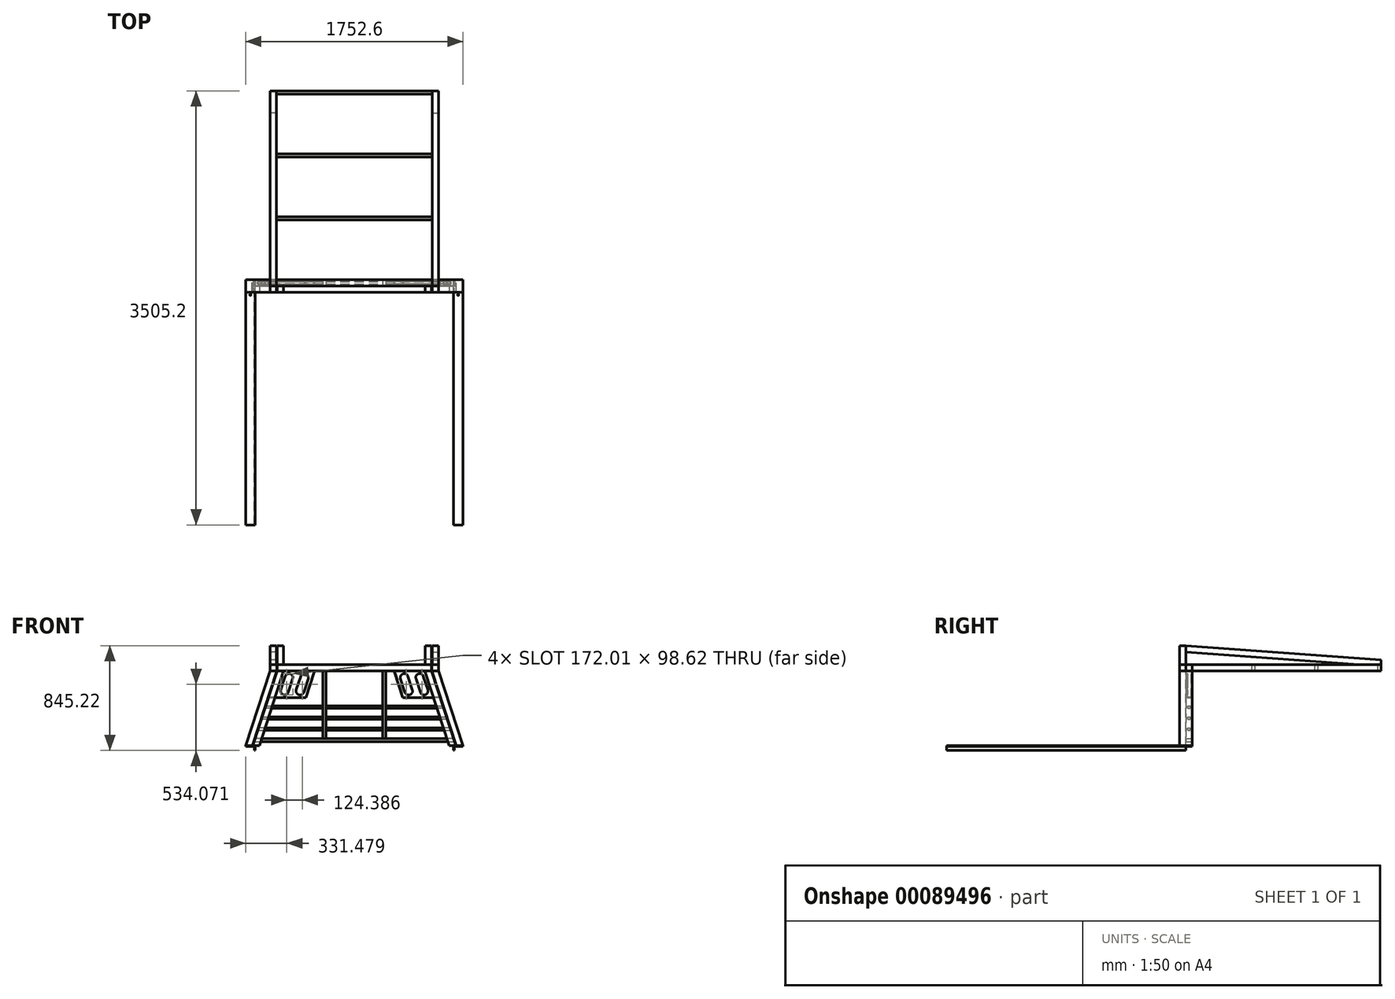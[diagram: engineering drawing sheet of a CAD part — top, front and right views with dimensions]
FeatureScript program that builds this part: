
annotation { "Feature Type Name" : "Feature", "Feature Type Description" : "" }
export const myFeature = defineFeature(function(context is Context, id is Id, definition is map)
    precondition{}
    {
        {
            var Q0;
            Q0=qCreatedBy(makeId("Front.planeOp"),FACE);
            var sketch = newSketch(context, id + "F0", { "sketchPlane" : qUnion([Q0])});
            skLineSegment(sketch, "E0", {"start": v(-876.3, 0) * mm, "end": v(-822.89, 0) * mm});
            skLineSegment(sketch, "E1", {"start": v(-822.89, 0) * mm, "end": v(-626.66, 603.92) * mm});
            skLineSegment(sketch, "E2", {"start": v(-626.66, 603.92) * mm, "end": v(-680.07, 603.92) * mm});
            skLineSegment(sketch, "E3", {"start": v(-680.07, 603.92) * mm, "end": v(-876.3, 0) * mm});
            skLineSegment(sketch, "E4", {"start": v(626.66, 603.92) * mm, "end": v(680.07, 603.92) * mm});
            skLineSegment(sketch, "E5", {"start": v(680.07, 603.92) * mm, "end": v(876.3, 0) * mm});
            skLineSegment(sketch, "E6", {"start": v(876.3, 0) * mm, "end": v(822.89, 0) * mm});
            skLineSegment(sketch, "E7", {"start": v(822.89, 0) * mm, "end": v(626.66, 603.92) * mm});
            skLineSegment(sketch, "E8", {"start": v(-822.89, 0) * mm, "end": v(822.89, 0) * mm, "construction": true});
            skSolve(sketch);
        }
        {
            var Q0;
            Q0 = qSketchRegion(id + "F0", true);
            extrude(context, id + "F1", {"entities" : qUnion([Q0]), "depth" : 76.2 * mm, "hasSecondDirection" : true, "secondDirectionOppositeDirection" : true, "secondDirectionDepth" : 25.4 * mm});
        }
        {
            var Q0;
            Q0=qCreatedBy(makeId("Front.planeOp"),FACE);
            var sketch = newSketch(context, id + "F2", { "sketchPlane" : qUnion([Q0])});
            skLineSegment(sketch, "E9", {"start": v(-680.07, 654.72) * mm, "end": v(680.07, 654.72) * mm});
            skLineSegment(sketch, "E10", {"start": v(680.07, 654.72) * mm, "end": v(680.07, 603.92) * mm});
            skLineSegment(sketch, "E11", {"start": v(680.07, 603.92) * mm, "end": v(-680.07, 603.92) * mm});
            skLineSegment(sketch, "E12", {"start": v(-680.07, 603.92) * mm, "end": v(-680.07, 654.72) * mm});
            skLineSegment(sketch, "E13", {"start": v(-812.57, 31.75) * mm, "end": v(812.57, 31.75) * mm});
            skLineSegment(sketch, "E14", {"start": v(812.57, 31.75) * mm, "end": v(804.32, 57.15) * mm});
            skLineSegment(sketch, "E15", {"start": v(804.32, 57.15) * mm, "end": v(-804.32, 57.15) * mm});
            skLineSegment(sketch, "E16", {"start": v(-804.32, 57.15) * mm, "end": v(-812.57, 31.75) * mm});
            skSolve(sketch);
        }
        {
            var Q0;
            Q0 = qSketchRegion(id + "F2", true);
            extrude(context, id + "F3", {"entities" : qUnion([Q0]), "depth" : 25.4 * mm, "hasSecondDirection" : true, "secondDirectionOppositeDirection" : true, "secondDirectionDepth" : 25.4 * mm});
        }
        {
            var Q0;
            Q0=makeQuery(id+"F1.opExtrude","CAP_FACE",FACE,{"disambiguationData":[OSD([sQuery(id+"F0.wireOp",EDGE,"E4"),sQuery(id+"F0.wireOp",EDGE,"E5"),sQuery(id+"F0.wireOp",EDGE,"E6"),sQuery(id+"F0.wireOp",EDGE,"E7")])],"isStart":true});
            var sketch = newSketch(context, id + "F4", { "sketchPlane" : qUnion([Q0])});
            skLineSegment(sketch, "E17", {"start": v(-626.66, 603.92) * mm, "end": v(-696.81, 388.02) * mm});
            skLineSegment(sketch, "E18", {"start": v(-696.81, 388.02) * mm, "end": v(-392.01, 388.02) * mm});
            skLineSegment(sketch, "E19", {"start": v(-392.01, 388.02) * mm, "end": v(-321.86, 603.92) * mm});
            skLineSegment(sketch, "E20", {"start": v(-321.86, 603.92) * mm, "end": v(-626.66, 603.92) * mm});
            skLineSegment(sketch, "E21", {"start": v(321.86, 603.92) * mm, "end": v(626.66, 603.92) * mm});
            skLineSegment(sketch, "E22", {"start": v(626.66, 603.92) * mm, "end": v(696.81, 388.02) * mm});
            skLineSegment(sketch, "E23", {"start": v(696.81, 388.02) * mm, "end": v(392.01, 388.02) * mm});
            skLineSegment(sketch, "E24", {"start": v(392.01, 388.02) * mm, "end": v(321.86, 603.92) * mm});
            skSolve(sketch);
        }
        {
            var Q0;
            Q0 = qSketchRegion(id + "F4", true);
            extrude(context, id + "F5", {"entities" : qUnion([Q0]), "oppositeDirection" : true, "depth" : 6.35 * mm});
        }
        {
            var Q0;
            Q0=makeQuery(id+"F5.opExtrude","CAP_FACE",FACE,{"disambiguationData":[OSD([sQuery(id+"F4.wireOp",EDGE,"E21"),sQuery(id+"F4.wireOp",EDGE,"E22"),sQuery(id+"F4.wireOp",EDGE,"E23"),sQuery(id+"F4.wireOp",EDGE,"E24")])],"isStart":false});
            var Q1;
            Q1=makeQuery(id+"F5.opExtrude","CAP_FACE",FACE,{"disambiguationData":[OSD([sQuery(id+"F4.wireOp",EDGE,"E17"),sQuery(id+"F4.wireOp",EDGE,"E18"),sQuery(id+"F4.wireOp",EDGE,"E19"),sQuery(id+"F4.wireOp",EDGE,"E20")])],"isStart":false});
            extrude(context, id + "F6", {"entities" : qUnion([Q0, Q1]), "depth" : 38.1 * mm, "hasSecondDirection" : true, "secondDirectionOppositeDirection" : false, "secondDirectionDepth" : 31.75 * mm});
        }
        {
            var Q0;
            Q0=makeQuery(id+"F5.opExtrude","CAP_FACE",FACE,{"disambiguationData":[OSD([sQuery(id+"F4.wireOp",EDGE,"E21"),sQuery(id+"F4.wireOp",EDGE,"E22"),sQuery(id+"F4.wireOp",EDGE,"E23"),sQuery(id+"F4.wireOp",EDGE,"E24")])],"isStart":false});
            var sketch = newSketch(context, id + "F7", { "sketchPlane" : qUnion([Q0])});
            skLineSegment(sketch, "E25", {"start": v(-321.86, 603.92) * mm, "end": v(-392.01, 388.02) * mm});
            skLineSegment(sketch, "E26", {"start": v(-392.01, 388.02) * mm, "end": v(-398.69, 388.02) * mm});
            skLineSegment(sketch, "E27", {"start": v(-398.69, 388.02) * mm, "end": v(-328.54, 603.92) * mm});
            skLineSegment(sketch, "E28", {"start": v(-328.54, 603.92) * mm, "end": v(-321.86, 603.92) * mm});
            skLineSegment(sketch, "E29", {"start": v(321.86, 603.92) * mm, "end": v(392.01, 388.02) * mm});
            skLineSegment(sketch, "E30", {"start": v(392.01, 388.02) * mm, "end": v(398.69, 388.02) * mm});
            skLineSegment(sketch, "E31", {"start": v(398.69, 388.02) * mm, "end": v(328.54, 603.92) * mm});
            skLineSegment(sketch, "E32", {"start": v(328.54, 603.92) * mm, "end": v(321.86, 603.92) * mm});
            skSolve(sketch);
        }
        {
            var Q0;
            Q0 = qSketchRegion(id + "F7", true);
            var Q1;
            Q1=makeQuery(id+"F6.opExtrude","CAP_FACE",FACE,{"disambiguationData":[OSD([sQuery(id+"F4.wireOp",EDGE,"E21"),sQuery(id+"F4.wireOp",EDGE,"E22"),sQuery(id+"F4.wireOp",EDGE,"E23"),sQuery(id+"F4.wireOp",EDGE,"E24")])],"isStart":true});
            extrude(context, id + "F8", {"entities" : qUnion([Q0]), "endBound" : BoundingType.UP_TO_SURFACE, "endBoundEntityFace" : qUnion([Q1]), "depth" : 25.4 * mm});
        }
        {
            var Q0;
            Q0=makeQuery(id+"F5.opExtrude","CAP_FACE",FACE,{"disambiguationData":[OSD([sQuery(id+"F4.wireOp",EDGE,"E21"),sQuery(id+"F4.wireOp",EDGE,"E22"),sQuery(id+"F4.wireOp",EDGE,"E23"),sQuery(id+"F4.wireOp",EDGE,"E24")])],"isStart":false});
            var sketch = newSketch(context, id + "F9", { "sketchPlane" : qUnion([Q0])});
            skLineSegment(sketch, "E33", {"start": v(-696.81, 388.02) * mm, "end": v(-398.69, 388.02) * mm});
            skLineSegment(sketch, "E34", {"start": v(-398.69, 388.02) * mm, "end": v(-396.62, 394.37) * mm});
            skLineSegment(sketch, "E35", {"start": v(-396.62, 394.37) * mm, "end": v(-694.75, 394.37) * mm});
            skLineSegment(sketch, "E36", {"start": v(-694.75, 394.37) * mm, "end": v(-696.81, 388.02) * mm});
            skLineSegment(sketch, "E37", {"start": v(398.69, 388.02) * mm, "end": v(696.81, 388.02) * mm});
            skLineSegment(sketch, "E38", {"start": v(696.81, 388.02) * mm, "end": v(694.75, 394.37) * mm});
            skLineSegment(sketch, "E39", {"start": v(694.75, 394.37) * mm, "end": v(396.62, 394.37) * mm});
            skLineSegment(sketch, "E40", {"start": v(396.62, 394.37) * mm, "end": v(398.69, 388.02) * mm});
            skSolve(sketch);
        }
        {
            var Q0;
            Q0 = qSketchRegion(id + "F9", true);
            extrude(context, id + "F10", {"entities" : qUnion([Q0]), "endBound" : BoundingType.UP_TO_NEXT, "depth" : 25.4 * mm});
        }
        {
            var Q0;
            Q0=makeQuery(id+"F6.opExtrude","CAP_FACE",FACE,{"disambiguationData":[OSD([sQuery(id+"F4.wireOp",EDGE,"E21"),sQuery(id+"F4.wireOp",EDGE,"E22"),sQuery(id+"F4.wireOp",EDGE,"E23"),sQuery(id+"F4.wireOp",EDGE,"E24")])],"isStart":false});
            var sketch = newSketch(context, id + "F11", { "sketchPlane" : qUnion([Q0])});
            skLineSegment(sketch, "E41", {"start": v(-438.1, 441.62) * mm, "end": v(-402.77, 550.32) * mm, "construction": true});
            skLineSegment(sketch, "E42", {"start": v(-562.48, 441.62) * mm, "end": v(-527.16, 550.32) * mm, "construction": true});
            skLineSegment(sketch, "E43", {"start": v(402.77, 550.32) * mm, "end": v(438.1, 441.62) * mm, "construction": true});
            skLineSegment(sketch, "E44", {"start": v(527.16, 550.32) * mm, "end": v(562.48, 441.62) * mm, "construction": true});
            skArc(sketch, "E45", {"start": v(-468.3, 451.43) * mm, "mid": v(-447.9, 411.42) * mm, "end": v(-407.9, 431.8) * mm});
            skArc(sketch, "E46", {"start": v(-372.58, 540.51) * mm, "mid": v(-392.96, 580.52) * mm, "end": v(-432.97, 560.14) * mm});
            skArc(sketch, "E47", {"start": v(-592.68, 451.43) * mm, "mid": v(-572.3, 411.42) * mm, "end": v(-532.29, 431.8) * mm});
            skArc(sketch, "E48", {"start": v(-496.96, 540.51) * mm, "mid": v(-517.35, 580.52) * mm, "end": v(-557.36, 560.14) * mm});
            skArc(sketch, "E49", {"start": v(432.97, 560.14) * mm, "mid": v(392.96, 580.52) * mm, "end": v(372.58, 540.51) * mm});
            skArc(sketch, "E50", {"start": v(407.9, 431.8) * mm, "mid": v(447.9, 411.42) * mm, "end": v(468.3, 451.43) * mm});
            skArc(sketch, "E51", {"start": v(557.36, 560.14) * mm, "mid": v(517.35, 580.52) * mm, "end": v(496.96, 540.51) * mm});
            skArc(sketch, "E52", {"start": v(532.29, 431.8) * mm, "mid": v(572.3, 411.42) * mm, "end": v(592.68, 451.43) * mm});
            skLineSegment(sketch, "E53", {"start": v(-468.3, 451.43) * mm, "end": v(-432.97, 560.14) * mm});
            skLineSegment(sketch, "E54", {"start": v(-372.58, 540.51) * mm, "end": v(-407.9, 431.8) * mm});
            skLineSegment(sketch, "E55", {"start": v(-532.29, 431.8) * mm, "end": v(-496.96, 540.51) * mm});
            skLineSegment(sketch, "E56", {"start": v(-592.68, 451.43) * mm, "end": v(-557.36, 560.14) * mm});
            skLineSegment(sketch, "E57", {"start": v(432.97, 560.14) * mm, "end": v(468.3, 451.43) * mm});
            skLineSegment(sketch, "E58", {"start": v(372.58, 540.51) * mm, "end": v(407.9, 431.8) * mm});
            skLineSegment(sketch, "E59", {"start": v(496.96, 540.51) * mm, "end": v(532.29, 431.8) * mm});
            skLineSegment(sketch, "E60", {"start": v(557.36, 560.14) * mm, "end": v(592.68, 451.43) * mm});
            skLineSegment(sketch, "E61", {"start": v(-608.32, 495.97) * mm, "end": v(-544.82, 495.97) * mm, "construction": true});
            skLineSegment(sketch, "E62", {"start": v(-544.82, 495.97) * mm, "end": v(-420.44, 495.97) * mm, "construction": true});
            skLineSegment(sketch, "E63", {"start": v(-420.44, 495.97) * mm, "end": v(-356.94, 495.97) * mm, "construction": true});
            skLineSegment(sketch, "E64", {"start": v(356.94, 495.97) * mm, "end": v(420.44, 495.97) * mm, "construction": true});
            skPoint(sketch, "E64.startSnap0", {"position": v(544.82, 495.97) * mm});
            skPoint(sketch, "E64.endSnap0", {"position": v(420.44, 495.97) * mm});
            skLineSegment(sketch, "E65", {"start": v(420.44, 495.97) * mm, "end": v(544.82, 495.97) * mm, "construction": true});
            skLineSegment(sketch, "E66", {"start": v(608.32, 495.97) * mm, "end": v(544.82, 495.97) * mm, "construction": true});
            skSolve(sketch);
        }
        {
            var Q0;
            Q0 = qSketchRegion(id + "F11", true);
            extrude(context, id + "F12", {"entities" : qUnion([Q0]), "operationType" : NewBodyOperationType.REMOVE, "endBound" : BoundingType.UP_TO_NEXT, "oppositeDirection" : true, "depth" : 25.4 * mm});
        }
        {
            var Q0;
            Q0=qCreatedBy(makeId("Front.planeOp"),FACE);
            var sketch = newSketch(context, id + "F13", { "sketchPlane" : qUnion([Q0])});
            skLineSegment(sketch, "E67", {"start": v(-782.08, 125.58) * mm, "end": v(782.08, 125.58) * mm});
            skLineSegment(sketch, "E68", {"start": v(782.08, 125.58) * mm, "end": v(775.9, 144.63) * mm});
            skLineSegment(sketch, "E69", {"start": v(775.9, 144.63) * mm, "end": v(-775.9, 144.63) * mm});
            skLineSegment(sketch, "E70", {"start": v(-775.9, 144.63) * mm, "end": v(-782.08, 125.58) * mm});
            skLineSegment(sketch, "E71", {"start": v(-753.66, 213.06) * mm, "end": v(-747.47, 232.11) * mm});
            skLineSegment(sketch, "E72", {"start": v(-747.47, 232.11) * mm, "end": v(747.47, 232.11) * mm});
            skLineSegment(sketch, "E73", {"start": v(747.47, 232.11) * mm, "end": v(753.66, 213.06) * mm});
            skLineSegment(sketch, "E74", {"start": v(753.66, 213.06) * mm, "end": v(-753.66, 213.06) * mm});
            skLineSegment(sketch, "E75", {"start": v(-725.23, 300.54) * mm, "end": v(-719.04, 319.6) * mm});
            skLineSegment(sketch, "E76", {"start": v(-719.04, 319.6) * mm, "end": v(719.04, 319.6) * mm});
            skLineSegment(sketch, "E77", {"start": v(719.04, 319.6) * mm, "end": v(725.23, 300.54) * mm});
            skLineSegment(sketch, "E78", {"start": v(725.23, 300.54) * mm, "end": v(-725.23, 300.54) * mm});
            skLineSegment(sketch, "E79", {"start": v(-392.01, 388.02) * mm, "end": v(392.01, 388.02) * mm, "construction": true});
            skLineSegment(sketch, "E80", {"start": v(0, 388.02) * mm, "end": v(0, 319.6) * mm, "construction": true});
            skLineSegment(sketch, "E81", {"start": v(0, 300.54) * mm, "end": v(0, 232.11) * mm, "construction": true});
            skLineSegment(sketch, "E82", {"start": v(0, 213.06) * mm, "end": v(0, 144.63) * mm, "construction": true});
            skLineSegment(sketch, "E83", {"start": v(0, 125.58) * mm, "end": v(0, 57.15) * mm, "construction": true});
            skSolve(sketch);
        }
        {
            var Q0;
            Q0 = qSketchRegion(id + "F13", true);
            extrude(context, id + "F14", {"entities" : qUnion([Q0]), "depth" : 9.52 * mm, "hasSecondDirection" : true, "secondDirectionOppositeDirection" : true, "secondDirectionDepth" : 9.52 * mm});
        }
        {
            var Q0;
            Q0=makeQuery(id+"F1.opExtrude","SWEPT_FACE",FACE,{"disambiguationData":[OSD([sQuery(id+"F0.wireOp",EDGE,"E0")])]});
            shell(context, id + "F15", {"entities" : qUnion([Q0]), "thickness" : 3.17 * mm});
        }
        {
            var Q0;
            Q0=makeQuery(id+"F1.opExtrude","CAP_FACE",FACE,{"disambiguationData":[OSD([sQuery(id+"F0.wireOp",EDGE,"E0"),sQuery(id+"F0.wireOp",EDGE,"E1"),sQuery(id+"F0.wireOp",EDGE,"E2"),sQuery(id+"F0.wireOp",EDGE,"E3")])],"isStart":true});
            var sketch = newSketch(context, id + "F16", { "sketchPlane" : qUnion([Q0])});
            skLineSegment(sketch, "E84", {"start": v(876.3, -6.35) * mm, "end": v(806.45, -6.35) * mm});
            skLineSegment(sketch, "E85", {"start": v(806.45, -6.35) * mm, "end": v(806.45, -38.1) * mm});
            skLineSegment(sketch, "E86", {"start": v(806.45, -38.1) * mm, "end": v(800.1, -38.1) * mm});
            skLineSegment(sketch, "E87", {"start": v(800.1, -38.1) * mm, "end": v(800.1, 0) * mm});
            skLineSegment(sketch, "E88", {"start": v(800.1, 0) * mm, "end": v(876.3, 0) * mm});
            skLineSegment(sketch, "E89", {"start": v(876.3, 0) * mm, "end": v(876.3, -6.35) * mm});
            skLineSegment(sketch, "E90", {"start": v(-876.3, 0) * mm, "end": v(-800.1, 0) * mm});
            skLineSegment(sketch, "E91", {"start": v(-800.1, 0) * mm, "end": v(-800.1, -38.1) * mm});
            skLineSegment(sketch, "E92", {"start": v(-800.1, -38.1) * mm, "end": v(-806.45, -38.1) * mm});
            skLineSegment(sketch, "E93", {"start": v(-806.45, -38.1) * mm, "end": v(-806.45, -6.35) * mm});
            skLineSegment(sketch, "E94", {"start": v(-806.45, -6.35) * mm, "end": v(-876.3, -6.35) * mm});
            skLineSegment(sketch, "E95", {"start": v(-876.3, -6.35) * mm, "end": v(-876.3, 0) * mm});
            skSolve(sketch);
        }
        {
            var Q0;
            Q0 = qSketchRegion(id + "F16", true);
            extrude(context, id + "F17", {"entities" : qUnion([Q0]), "oppositeDirection" : true, "depth" : 1828.8 * mm + 152.4 * mm});
        }
        {
            var Q0;
            Q0=makeQuery(id+"F17.opExtrude","SWEPT_FACE",FACE,{"disambiguationData":[OSD([sQuery(id+"F16.wireOp",EDGE,"E93")])]});
            var sketch = newSketch(context, id + "F18", { "sketchPlane" : qUnion([Q0])});
            skLineSegment(sketch, "E96.bottom", {"start": v(25.4, -38.1) * mm, "end": v(-25.4, -38.1) * mm});
            skLineSegment(sketch, "E96.top", {"start": v(25.4, -6.35) * mm, "end": v(-25.4, -6.35) * mm});
            skLineSegment(sketch, "E96.left", {"start": v(25.4, -38.1) * mm, "end": v(25.4, -6.35) * mm});
            skLineSegment(sketch, "E96.right", {"start": v(-25.4, -38.1) * mm, "end": v(-25.4, -6.35) * mm});
            skSolve(sketch);
        }
        {
            var Q0;
            Q0 = qSketchRegion(id + "F18", true);
            extrude(context, id + "F19", {"entities" : qUnion([Q0]), "operationType" : NewBodyOperationType.REMOVE, "endBound" : BoundingType.THROUGH_ALL, "oppositeDirection" : true, "depth" : 25.4 * mm});
        }
        {
            var Q0;
            Q0=makeQuery(id+"F17.opExtrude","SWEPT_FACE",FACE,{"disambiguationData":[OSD([sQuery(id+"F16.wireOp",EDGE,"E95")])]});
            var Q1;
            Q1=makeQuery(id+"F17.opExtrude","SWEPT_FACE",FACE,{"disambiguationData":[OSD([sQuery(id+"F16.wireOp",EDGE,"E91")])]});
            cPlane(context, id + "F20", {"entities" : qUnion([Q0, Q1]), "cplaneType" : CPlaneType.MID_PLANE, "offset" : 25.4 * mm, "width" : 152.4 * mm, "height" : 152.4 * mm});
        }
        {
            var Q0;
            Q0=makeQuery(id+"F17.opExtrude","SWEPT_FACE",FACE,{"disambiguationData":[OSD([sQuery(id+"F16.wireOp",EDGE,"E87")])]});
            var Q1;
            Q1=makeQuery(id+"F17.opExtrude","SWEPT_FACE",FACE,{"disambiguationData":[OSD([sQuery(id+"F16.wireOp",EDGE,"E89")])]});
            cPlane(context, id + "F21", {"entities" : qUnion([Q0, Q1]), "cplaneType" : CPlaneType.MID_PLANE, "offset" : 25.4 * mm, "width" : 152.4 * mm, "height" : 152.4 * mm});
        }
        {
            var Q0;
            Q0=makeQuery(id+"F19.boolean.opBoolean","MERGE",FACE,{"derivedFrom":[makeQuery(id+"F17.opExtrude","SWEPT_FACE",FACE,{"disambiguationData":[OSD([sQuery(id+"F16.wireOp",EDGE,"E94")])]}),makeQuery(id+"F19.opExtrude","SWEPT_FACE",FACE,{"disambiguationData":[OSD([sQuery(id+"F18.wireOp",EDGE,"E96.top")])]})]});
            var sketch = newSketch(context, id + "F22", { "sketchPlane" : qUnion([Q0])});
            skCircle(sketch, "E97", {"center": v(-838.2, 98.42) * mm, "radius": 5.04 * mm});
            skCircle(sketch, "E98", {"center": v(838.2, 98.43) * mm, "radius": 5.04 * mm});
            skLineSegment(sketch, "E99", {"start": v(-838.2, 98.42) * mm, "end": v(838.2, 98.43) * mm, "construction": true});
            skLineSegment(sketch, "E100", {"start": v(0, 98.43) * mm, "end": v(0, -25.4) * mm, "construction": true});
            skSolve(sketch);
        }
        {
            var Q0;
            Q0 = qSketchRegion(id + "F22", true);
            extrude(context, id + "F23", {"entities" : qUnion([Q0]), "operationType" : NewBodyOperationType.REMOVE, "endBound" : BoundingType.UP_TO_NEXT, "oppositeDirection" : true, "depth" : 25.4 * mm});
        }
        {
            var Q0;
            Q0=makeQuery(id+"F3.opExtrude","CAP_FACE",FACE,{"disambiguationData":[OSD([sQuery(id+"F2.wireOp",EDGE,"E9"),sQuery(id+"F2.wireOp",EDGE,"E10"),sQuery(id+"F2.wireOp",EDGE,"E11"),sQuery(id+"F2.wireOp",EDGE,"E12")])],"isStart":false});
            var sketch = newSketch(context, id + "F24", { "sketchPlane" : qUnion([Q0])});
            skLineSegment(sketch, "E101.bottom", {"start": v(-680.07, 654.72) * mm, "end": v(-626.66, 654.72) * mm});
            skLineSegment(sketch, "E101.top", {"start": v(-680.07, 603.92) * mm, "end": v(-626.66, 603.92) * mm});
            skLineSegment(sketch, "E101.left", {"start": v(-680.07, 654.72) * mm, "end": v(-680.07, 603.92) * mm});
            skLineSegment(sketch, "E101.right", {"start": v(-626.66, 654.72) * mm, "end": v(-626.66, 603.92) * mm});
            skLineSegment(sketch, "E102.bottom", {"start": v(680.07, 603.92) * mm, "end": v(626.66, 603.92) * mm});
            skLineSegment(sketch, "E102.top", {"start": v(680.07, 654.72) * mm, "end": v(626.66, 654.72) * mm});
            skLineSegment(sketch, "E102.left", {"start": v(680.07, 603.92) * mm, "end": v(680.07, 654.72) * mm});
            skLineSegment(sketch, "E102.right", {"start": v(626.66, 603.92) * mm, "end": v(626.66, 654.72) * mm});
            skSolve(sketch);
        }
        {
            var Q0;
            Q0 = qSketchRegion(id + "F24", true);
            extrude(context, id + "F25", {"entities" : qUnion([Q0]), "depth" : 50.8 * mm});
        }
        {
            var Q0;
            Q0=makeQuery(id+"F25.opExtrude","CAP_FACE",FACE,{"disambiguationData":[OSD([sQuery(id+"F24.wireOp",EDGE,"E101.bottom"),sQuery(id+"F24.wireOp",EDGE,"E101.top"),sQuery(id+"F24.wireOp",EDGE,"E101.left"),sQuery(id+"F24.wireOp",EDGE,"E101.right")])],"isStart":false});
            var sketch = newSketch(context, id + "F26", { "sketchPlane" : qUnion([Q0])});
            skLineSegment(sketch, "E103.bottom", {"start": v(-680.07, 654.72) * mm, "end": v(-629.27, 654.72) * mm});
            skLineSegment(sketch, "E103.top", {"start": v(-680.07, 807.12) * mm, "end": v(-629.27, 807.12) * mm});
            skLineSegment(sketch, "E103.left", {"start": v(-680.07, 654.72) * mm, "end": v(-680.07, 807.12) * mm});
            skLineSegment(sketch, "E103.right", {"start": v(-629.27, 654.72) * mm, "end": v(-629.27, 807.12) * mm});
            skLineSegment(sketch, "E104.bottom", {"start": v(680.07, 654.72) * mm, "end": v(629.27, 654.72) * mm});
            skLineSegment(sketch, "E104.top", {"start": v(680.07, 807.12) * mm, "end": v(629.27, 807.12) * mm});
            skLineSegment(sketch, "E104.left", {"start": v(680.07, 654.72) * mm, "end": v(680.07, 807.12) * mm});
            skLineSegment(sketch, "E104.right", {"start": v(629.27, 654.72) * mm, "end": v(629.27, 807.12) * mm});
            skSolve(sketch);
        }
        {
            var Q0;
            Q0 = qSketchRegion(id + "F26", true);
            extrude(context, id + "F27", {"entities" : qUnion([Q0]), "oppositeDirection" : true, "depth" : 50.8 * mm});
        }
        {
            var Q0;
            Q0=makeQuery(id+"F27.opExtrude","SWEPT_FACE",FACE,{"disambiguationData":[OSD([sQuery(id+"F26.wireOp",EDGE,"E104.left")])]});
            var sketch = newSketch(context, id + "F28", { "sketchPlane" : qUnion([Q0])});
            skLineSegment(sketch, "E105.bottom", {"start": v(25.4, 603.92) * mm, "end": v(1549.4, 603.92) * mm});
            skLineSegment(sketch, "E105.top", {"start": v(25.4, 654.72) * mm, "end": v(1549.4, 654.72) * mm});
            skLineSegment(sketch, "E105.left", {"start": v(25.4, 603.92) * mm, "end": v(25.4, 654.72) * mm});
            skLineSegment(sketch, "E105.right", {"start": v(1549.4, 603.92) * mm, "end": v(1549.4, 654.72) * mm});
            skSolve(sketch);
        }
        {
            var Q0;
            Q0 = qSketchRegion(id + "F28", true);
            extrude(context, id + "F29", {"entities" : qUnion([Q0]), "oppositeDirection" : true, "depth" : 50.8 * mm});
        }
        {
            var Q0;
            Q0=makeQuery(id+"F29.opExtrude","CAP_FACE",FACE,{"disambiguationData":[OSD([sQuery(id+"F28.wireOp",EDGE,"E105.bottom"),sQuery(id+"F28.wireOp",EDGE,"E105.top"),sQuery(id+"F28.wireOp",EDGE,"E105.left"),sQuery(id+"F28.wireOp",EDGE,"E105.right")])],"isStart":true});
            var sketch = newSketch(context, id + "F30", { "sketchPlane" : qUnion([Q0])});
            skLineSegment(sketch, "E106", {"start": v(1372.58, 654.72) * mm, "end": v(-25.4, 756.19) * mm});
            skLineSegment(sketch, "E107", {"start": v(-25.4, 756.19) * mm, "end": v(-25.4, 807.12) * mm});
            skLineSegment(sketch, "E108", {"start": v(-25.4, 807.12) * mm, "end": v(1549.4, 692.82) * mm});
            skLineSegment(sketch, "E109", {"start": v(1549.4, 692.82) * mm, "end": v(1549.4, 654.72) * mm});
            skLineSegment(sketch, "E110", {"start": v(1549.4, 654.72) * mm, "end": v(1372.58, 654.72) * mm});
            skSolve(sketch);
        }
        {
            var Q0;
            Q0 = qSketchRegion(id + "F30", true);
            extrude(context, id + "F31", {"entities" : qUnion([Q0]), "oppositeDirection" : true, "depth" : 50.8 * mm});
        }
        {
            var Q0;
            Q0=makeQuery(id+"F31.opExtrude","SWEPT_BODY",BODY,{"disambiguationData":[OSD([sQuery(id+"F30.wireOp",EDGE,"E106"),sQuery(id+"F30.wireOp",EDGE,"E107"),sQuery(id+"F30.wireOp",EDGE,"E108"),sQuery(id+"F30.wireOp",EDGE,"E109"),sQuery(id+"F30.wireOp",EDGE,"E110")])]});
            var Q1;
            Q1=makeQuery(id+"F29.opExtrude","SWEPT_BODY",BODY,{"disambiguationData":[OSD([sQuery(id+"F28.wireOp",EDGE,"E105.bottom"),sQuery(id+"F28.wireOp",EDGE,"E105.top"),sQuery(id+"F28.wireOp",EDGE,"E105.left"),sQuery(id+"F28.wireOp",EDGE,"E105.right")])]});
            var Q2;
            Q2=qCreatedBy(makeId("Right.planeOp"),FACE);
            mirror(context, id + "F32", {"entities" : qUnion([Q0, Q1]), "mirrorPlane" : qUnion([Q2])});
        }
        {
            var Q0;
            Q0=makeQuery(id+"F29.opExtrude","CAP_FACE",FACE,{"disambiguationData":[OSD([sQuery(id+"F28.wireOp",EDGE,"E105.bottom"),sQuery(id+"F28.wireOp",EDGE,"E105.top"),sQuery(id+"F28.wireOp",EDGE,"E105.left"),sQuery(id+"F28.wireOp",EDGE,"E105.right")])],"isStart":false});
            var sketch = newSketch(context, id + "F33", { "sketchPlane" : qUnion([Q0])});
            skLineSegment(sketch, "E111.bottom", {"start": v(-508, 603.92) * mm, "end": v(-533.4, 603.92) * mm});
            skLineSegment(sketch, "E111.top", {"start": v(-508, 654.72) * mm, "end": v(-533.4, 654.72) * mm});
            skLineSegment(sketch, "E111.left", {"start": v(-508, 603.92) * mm, "end": v(-508, 654.72) * mm});
            skLineSegment(sketch, "E111.right", {"start": v(-533.4, 603.92) * mm, "end": v(-533.4, 654.72) * mm});
            skLineSegment(sketch, "E112.bottom", {"start": v(-1016, 603.92) * mm, "end": v(-1041.4, 603.92) * mm});
            skLineSegment(sketch, "E112.top", {"start": v(-1016, 654.72) * mm, "end": v(-1041.4, 654.72) * mm});
            skLineSegment(sketch, "E112.left", {"start": v(-1041.4, 603.92) * mm, "end": v(-1041.4, 654.72) * mm});
            skLineSegment(sketch, "E112.right", {"start": v(-1016, 603.92) * mm, "end": v(-1016, 654.72) * mm});
            skLineSegment(sketch, "E113.bottom", {"start": v(-1549.4, 603.92) * mm, "end": v(-1524, 603.92) * mm});
            skLineSegment(sketch, "E113.top", {"start": v(-1549.4, 654.72) * mm, "end": v(-1524, 654.72) * mm});
            skLineSegment(sketch, "E113.left", {"start": v(-1549.4, 603.92) * mm, "end": v(-1549.4, 654.72) * mm});
            skLineSegment(sketch, "E113.right", {"start": v(-1524, 603.92) * mm, "end": v(-1524, 654.72) * mm});
            skLineSegment(sketch, "E114", {"start": v(-25.4, 603.92) * mm, "end": v(-508, 603.92) * mm, "construction": true});
            skLineSegment(sketch, "E115", {"start": v(-533.4, 603.92) * mm, "end": v(-1016, 603.92) * mm, "construction": true});
            skLineSegment(sketch, "E116", {"start": v(-1041.4, 603.92) * mm, "end": v(-1524, 603.92) * mm, "construction": true});
            skSolve(sketch);
        }
        {
            var Q0;
            Q0 = qSketchRegion(id + "F33", true);
            extrude(context, id + "F34", {"entities" : qUnion([Q0]), "endBound" : BoundingType.UP_TO_NEXT, "depth" : 25.4 * mm});
        }
        {
            var Q0;
            Q0=makeQuery(id+"F3.opExtrude","SWEPT_FACE",FACE,{"disambiguationData":[OSD([sQuery(id+"F2.wireOp",EDGE,"E15")])]});
            var sketch = newSketch(context, id + "F35", { "sketchPlane" : qUnion([Q0])});
            skLineSegment(sketch, "E117.bottom", {"start": v(-254, -25.4) * mm, "end": v(-228.6, -25.4) * mm});
            skLineSegment(sketch, "E117.top", {"start": v(-254, 25.4) * mm, "end": v(-228.6, 25.4) * mm});
            skLineSegment(sketch, "E117.left", {"start": v(-254, -25.4) * mm, "end": v(-254, 25.4) * mm});
            skLineSegment(sketch, "E117.right", {"start": v(-228.6, -25.4) * mm, "end": v(-228.6, 25.4) * mm});
            skLineSegment(sketch, "E118.bottom", {"start": v(228.6, -25.4) * mm, "end": v(254, -25.4) * mm});
            skLineSegment(sketch, "E118.top", {"start": v(228.6, 25.4) * mm, "end": v(254, 25.4) * mm});
            skLineSegment(sketch, "E118.left", {"start": v(228.6, -25.4) * mm, "end": v(228.6, 25.4) * mm});
            skLineSegment(sketch, "E118.right", {"start": v(254, -25.4) * mm, "end": v(254, 25.4) * mm});
            skLineSegment(sketch, "E119", {"start": v(-228.6, -25.4) * mm, "end": v(0, -25.4) * mm, "construction": true});
            skLineSegment(sketch, "E120", {"start": v(0, -25.4) * mm, "end": v(228.6, -25.4) * mm, "construction": true});
            skSolve(sketch);
        }
        {
            var Q0;
            Q0 = qSketchRegion(id + "F35", true);
            var Q1;
            Q1=makeQuery(id+"F3.opExtrude","SWEPT_FACE",FACE,{"disambiguationData":[OSD([sQuery(id+"F2.wireOp",EDGE,"E11")])]});
            extrude(context, id + "F36", {"entities" : qUnion([Q0]), "endBound" : BoundingType.UP_TO_SURFACE, "endBoundEntityFace" : qUnion([Q1]), "depth" : 25.4 * mm});
        }
        {
            var Q0;
            Q0=makeQuery(id+"F36.opExtrude","SWEPT_BODY",BODY,{"disambiguationData":[OSD([sQuery(id+"F35.wireOp",EDGE,"E117.bottom"),sQuery(id+"F35.wireOp",EDGE,"E117.top"),sQuery(id+"F35.wireOp",EDGE,"E117.left"),sQuery(id+"F35.wireOp",EDGE,"E117.right")])]});
            var Q1;
            Q1=makeQuery(id+"F36.opExtrude","SWEPT_BODY",BODY,{"disambiguationData":[OSD([sQuery(id+"F35.wireOp",EDGE,"E118.bottom"),sQuery(id+"F35.wireOp",EDGE,"E118.top"),sQuery(id+"F35.wireOp",EDGE,"E118.left"),sQuery(id+"F35.wireOp",EDGE,"E118.right")])]});
            var Q2;
            Q2=makeQuery(id+"F14.opExtrude","SWEPT_BODY",BODY,{"disambiguationData":[OSD([sQuery(id+"F13.wireOp",EDGE,"E67"),sQuery(id+"F13.wireOp",EDGE,"E68"),sQuery(id+"F13.wireOp",EDGE,"E69"),sQuery(id+"F13.wireOp",EDGE,"E70")])]});
            var Q3;
            Q3=makeQuery(id+"F14.opExtrude","SWEPT_BODY",BODY,{"disambiguationData":[OSD([sQuery(id+"F13.wireOp",EDGE,"E71"),sQuery(id+"F13.wireOp",EDGE,"E72"),sQuery(id+"F13.wireOp",EDGE,"E73"),sQuery(id+"F13.wireOp",EDGE,"E74")])]});
            var Q4;
            Q4=makeQuery(id+"F14.opExtrude","SWEPT_BODY",BODY,{"disambiguationData":[OSD([sQuery(id+"F13.wireOp",EDGE,"E75"),sQuery(id+"F13.wireOp",EDGE,"E76"),sQuery(id+"F13.wireOp",EDGE,"E77"),sQuery(id+"F13.wireOp",EDGE,"E78")])]});
            booleanBodies(context, id + "F37", {"operationType" : BooleanOperationType.SUBTRACTION, "tools" : qUnion([Q0, Q1]), "targets" : qUnion([Q2, Q3, Q4])});
        }
        {
            var Q0;
            Q0 = qSketchRegion(id + "F35", true);
            var Q1;
            Q1=makeQuery(id+"F3.opExtrude","SWEPT_FACE",FACE,{"disambiguationData":[OSD([sQuery(id+"F2.wireOp",EDGE,"E11")])]});
            extrude(context, id + "F38", {"entities" : qUnion([Q0]), "endBound" : BoundingType.UP_TO_SURFACE, "endBoundEntityFace" : qUnion([Q1]), "depth" : 25.4 * mm});
        }
        {
            var Q0;
            Q0=makeQuery(id+"F1.opExtrude","CAP_FACE",FACE,{"disambiguationData":[OSD([sQuery(id+"F0.wireOp",EDGE,"E0"),sQuery(id+"F0.wireOp",EDGE,"E1"),sQuery(id+"F0.wireOp",EDGE,"E2"),sQuery(id+"F0.wireOp",EDGE,"E3")])],"isStart":false});
            var sketch = newSketch(context, id + "F39", { "sketchPlane" : qUnion([Q0])});
            skLineSegment(sketch, "E121", {"start": v(-819.55, 0) * mm, "end": v(-766.13, 0) * mm});
            skLineSegment(sketch, "E122", {"start": v(-766.13, 0) * mm, "end": v(-569.9, 603.92) * mm});
            skLineSegment(sketch, "E123", {"start": v(-569.9, 603.92) * mm, "end": v(-623.32, 603.92) * mm});
            skLineSegment(sketch, "E124", {"start": v(-623.32, 603.92) * mm, "end": v(-819.55, 0) * mm});
            skLineSegment(sketch, "E125", {"start": v(569.9, 603.92) * mm, "end": v(623.32, 603.92) * mm});
            skLineSegment(sketch, "E126", {"start": v(623.32, 603.92) * mm, "end": v(819.55, 0) * mm});
            skLineSegment(sketch, "E127", {"start": v(819.55, 0) * mm, "end": v(766.13, 0) * mm});
            skLineSegment(sketch, "E128", {"start": v(766.13, 0) * mm, "end": v(569.9, 603.92) * mm});
            skSolve(sketch);
        }
        {
            var Q0;
            Q0 = qSketchRegion(id + "F39", true);
            extrude(context, id + "F40", {"entities" : qUnion([Q0]), "oppositeDirection" : true, "depth" : 50.8 * mm});
        }
        {
            var Q0;
            Q0=makeQuery(id+"F40.opExtrude","CAP_FACE",FACE,{"disambiguationData":[OSD([sQuery(id+"F39.wireOp",EDGE,"E121"),sQuery(id+"F39.wireOp",EDGE,"E122"),sQuery(id+"F39.wireOp",EDGE,"E123"),sQuery(id+"F39.wireOp",EDGE,"E124")])],"isStart":true});
            var sketch = newSketch(context, id + "F41", { "sketchPlane" : qUnion([Q0])});
            skLineSegment(sketch, "E129.bottom", {"start": v(-623.32, 603.92) * mm, "end": v(623.32, 603.92) * mm});
            skLineSegment(sketch, "E129.top", {"start": v(-623.32, 654.72) * mm, "end": v(623.32, 654.72) * mm});
            skLineSegment(sketch, "E129.left", {"start": v(-623.32, 603.92) * mm, "end": v(-623.32, 654.72) * mm});
            skLineSegment(sketch, "E129.right", {"start": v(623.32, 603.92) * mm, "end": v(623.32, 654.72) * mm});
            skSolve(sketch);
        }
        {
            var Q0;
            Q0 = qSketchRegion(id + "F41", true);
            extrude(context, id + "F42", {"entities" : qUnion([Q0]), "oppositeDirection" : true, "depth" : 50.8 * mm});
        }
        {
            var Q0;
            Q0=makeQuery(id+"F42.opExtrude","CAP_FACE",FACE,{"disambiguationData":[OSD([sQuery(id+"F41.wireOp",EDGE,"E129.bottom"),sQuery(id+"F41.wireOp",EDGE,"E129.top"),sQuery(id+"F41.wireOp",EDGE,"E129.left"),sQuery(id+"F41.wireOp",EDGE,"E129.right")])],"isStart":true});
            var sketch = newSketch(context, id + "F43", { "sketchPlane" : qUnion([Q0])});
            skLineSegment(sketch, "E130.bottom", {"start": v(623.32, 654.72) * mm, "end": v(572.52, 654.72) * mm});
            skLineSegment(sketch, "E130.top", {"start": v(623.32, 807.12) * mm, "end": v(572.52, 807.12) * mm});
            skLineSegment(sketch, "E130.left", {"start": v(623.32, 654.72) * mm, "end": v(623.32, 807.12) * mm});
            skLineSegment(sketch, "E130.right", {"start": v(572.52, 654.72) * mm, "end": v(572.52, 807.12) * mm});
            skLineSegment(sketch, "E131.bottom", {"start": v(-623.32, 654.72) * mm, "end": v(-572.52, 654.72) * mm});
            skLineSegment(sketch, "E131.top", {"start": v(-623.32, 807.12) * mm, "end": v(-572.52, 807.12) * mm});
            skLineSegment(sketch, "E131.left", {"start": v(-623.32, 654.72) * mm, "end": v(-623.32, 807.12) * mm});
            skLineSegment(sketch, "E131.right", {"start": v(-572.52, 654.72) * mm, "end": v(-572.52, 807.12) * mm});
            skSolve(sketch);
        }
        {
            var Q0;
            Q0 = qSketchRegion(id + "F43", true);
            extrude(context, id + "F44", {"entities" : qUnion([Q0]), "oppositeDirection" : true, "depth" : 50.8 * mm});
        }
    });
